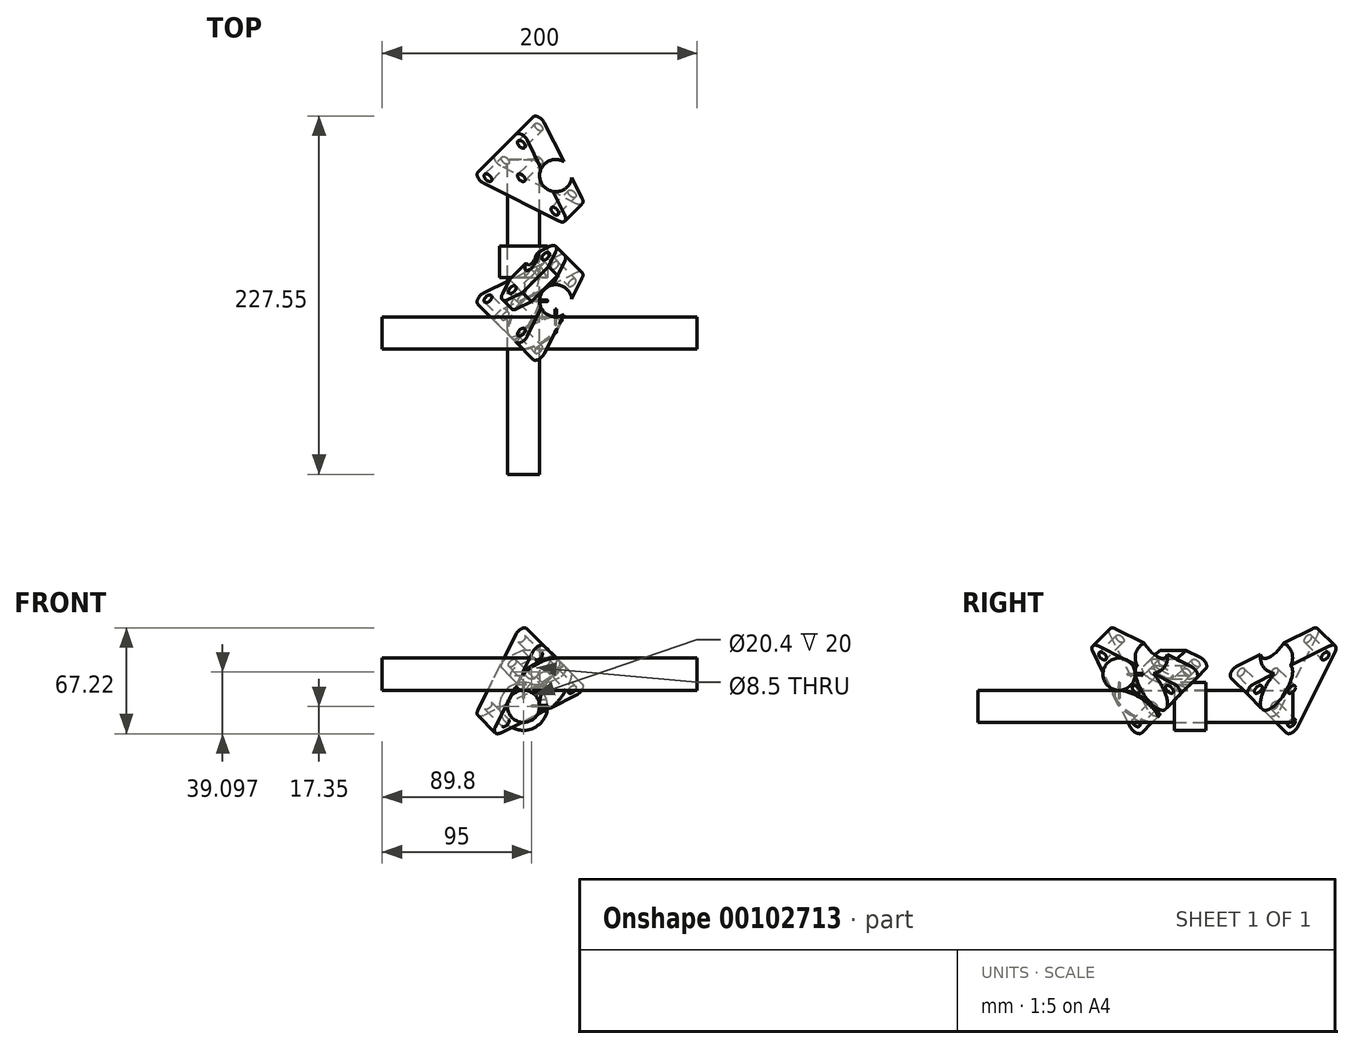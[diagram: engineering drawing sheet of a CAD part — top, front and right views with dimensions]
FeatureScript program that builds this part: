
annotation { "Feature Type Name" : "Feature", "Feature Type Description" : "" }
export const myFeature = defineFeature(function(context is Context, id is Id, definition is map)
    precondition{}
    {
        {
            var Q0;
            Q0=qCreatedBy(makeId("Top.planeOp"),FACE);
            var sketch = newSketch(context, id + "F0", { "sketchPlane" : qUnion([Q0])});
            skCircle(sketch, "E0", {"center": v(10.25, 10.25) * mm, "radius": 10.25 * mm});
            skLineSegment(sketch, "E1", {"start": v(3, 3) * mm, "end": v(14.79, -8.78) * mm, "construction": true});
            skLineSegment(sketch, "E2", {"start": v(30.79, 4.2) * mm, "end": v(17.5, 17.5) * mm, "construction": true});
            skLineSegment(sketch, "E3", {"start": v(0, 0) * mm, "end": v(17.5, 17.5) * mm, "construction": true});
            skLineSegment(sketch, "E4", {"start": v(14.79, -8.78) * mm, "end": v(30.79, 4.2) * mm, "construction": true});
            skSolve(sketch);
        }
        {
            var Q0;
            Q0=qSketchRegion(id+"F0",true);
            extrude(context, id + "F1", {"entities" : qUnion([Q0]), "endBound" : BoundingType.SYMMETRIC, "depth" : 200 * mm});
        }
        {
            var Q0;
            Q0=qCreatedBy(makeId("Right.planeOp"),FACE);
            var sketch = newSketch(context, id + "F2", { "sketchPlane" : qUnion([Q0])});
            skCircle(sketch, "E5", {"center": v(-10.25, 10.25) * mm, "radius": 10.25 * mm});
            skLineSegment(sketch, "E6", {"start": v(0, 0) * mm, "end": v(-17.5, 17.5) * mm, "construction": true});
            skLineSegment(sketch, "E7", {"start": v(-3, 3) * mm, "end": v(-20.36, -14.35) * mm, "construction": true});
            skLineSegment(sketch, "E8", {"start": v(-20.36, -14.35) * mm, "end": v(-34.85, 0.14) * mm, "construction": true});
            skLineSegment(sketch, "E9", {"start": v(-34.85, 0.14) * mm, "end": v(-17.5, 17.5) * mm, "construction": true});
            skSolve(sketch);
        }
        {
            var Q0;
            Q0=qSketchRegion(id+"F2",true);
            extrude(context, id + "F3", {"entities" : qUnion([Q0]), "endBound" : BoundingType.SYMMETRIC, "depth" : 200 * mm});
        }
        {
            var Q0;
            Q0=qCreatedBy(makeId("Front.planeOp"),FACE);
            var sketch = newSketch(context, id + "F4", { "sketchPlane" : qUnion([Q0])});
            skCircle(sketch, "E10", {"center": v(-10.2, -10.2) * mm, "radius": 10.2 * mm});
            skLineSegment(sketch, "E11", {"start": v(0, 0) * mm, "end": v(-17.41, -17.41) * mm, "construction": true});
            skLineSegment(sketch, "E12", {"start": v(-2.99, -2.99) * mm, "end": v(15.73, -21.7) * mm, "construction": true});
            skLineSegment(sketch, "E13", {"start": v(15.73, -21.7) * mm, "end": v(1.3, -36.13) * mm, "construction": true});
            skLineSegment(sketch, "E14", {"start": v(1.3, -36.13) * mm, "end": v(-17.41, -17.41) * mm, "construction": true});
            skSolve(sketch);
        }
        {
            var Q0;
            Q0=qSketchRegion(id+"F4",true);
            extrude(context, id + "F5", {"entities" : qUnion([Q0]), "endBound" : BoundingType.SYMMETRIC, "depth" : 200 * mm});
        }
        {
            var Q0;
            Q0=sQuery(id+"F2.wireOp",VERTEX,"E5.center");
            var Q1;
            Q1=sQuery(id+"F4.wireOp",VERTEX,"E10.center");
            var Q2;
            Q2=sQuery(id+"F0.wireOp",VERTEX,"E0.center");
            cPlane(context, id + "F6", {"entities" : qUnion([Q0, Q1, Q2]), "cplaneType" : CPlaneType.THREE_POINT, "offset" : 150 * mm, "width" : 150 * mm, "height" : 150 * mm});
        }
        {
            var Q0;
            Q0=qCreatedBy(makeId("Top.planeOp"),FACE);
            var sketch = newSketch(context, id + "F7", { "sketchPlane" : qUnion([Q0])});
            skLineSegment(sketch, "E15", {"start": v(-20.4, -100) * mm, "end": v(-20.4, 100) * mm});
            skLineSegment(sketch, "E16", {"start": v(0, 100) * mm, "end": v(0, -100) * mm});
            skLineSegment(sketch, "E17", {"start": v(100, -20.5) * mm, "end": v(-100, -20.5) * mm});
            skLineSegment(sketch, "E18", {"start": v(-100, 0) * mm, "end": v(100, 0) * mm});
            skLineSegment(sketch, "E19", {"start": v(-20.4, -20.5) * mm, "end": v(0, 0) * mm, "construction": true});
            skCircle(sketch, "E20", {"center": v(-10.2, -10.25) * mm, "radius": 0.5 * mm});
            skSolve(sketch);
        }
        {
            var Q0;
            Q0=makeQuery(id+"F7.imprint","IMPRINT",FACE,{"disambiguationData":[TD([[makeQuery(id+"F7.imprint","IMPRINT",EDGE,{"derivedFrom":sQuery(id+"F7.wireOp",EDGE,"E20")}),1.0]])]});
            extrude(context, id + "F8", {"entities" : qUnion([Q0]), "endBound" : BoundingType.SYMMETRIC, "depth" : 10 * mm});
        }
        {
            var Q0;
            Q0=qCreatedBy(makeId("Right.planeOp"),FACE);
            var sketch = newSketch(context, id + "F9", { "sketchPlane" : qUnion([Q0])});
            skLineSegment(sketch, "E21", {"start": v(100, -20.4) * mm, "end": v(-100, -20.4) * mm});
            skLineSegment(sketch, "E22", {"start": v(-100, 0) * mm, "end": v(100, 0) * mm});
            skLineSegment(sketch, "E23", {"start": v(20.5, 100) * mm, "end": v(20.5, -100) * mm});
            skLineSegment(sketch, "E24", {"start": v(0, -100) * mm, "end": v(0, 100) * mm});
            skLineSegment(sketch, "E25", {"start": v(20.5, -20.4) * mm, "end": v(0, 0) * mm, "construction": true});
            skCircle(sketch, "E26", {"center": v(10.25, -10.2) * mm, "radius": 0.5 * mm});
            skSolve(sketch);
        }
        {
            var Q0;
            Q0=makeQuery(id+"F9.imprint","IMPRINT",FACE,{"disambiguationData":[TD([[makeQuery(id+"F9.imprint","IMPRINT",EDGE,{"derivedFrom":sQuery(id+"F9.wireOp",EDGE,"E26")}),1.0]])]});
            extrude(context, id + "F10", {"entities" : qUnion([Q0]), "endBound" : BoundingType.SYMMETRIC, "depth" : 10 * mm});
        }
        {
            var Q0;
            Q0=qCreatedBy(makeId("Front.planeOp"),FACE);
            var sketch = newSketch(context, id + "F11", { "sketchPlane" : qUnion([Q0])});
            skLineSegment(sketch, "E27", {"start": v(0, -100) * mm, "end": v(0, 100) * mm});
            skLineSegment(sketch, "E28", {"start": v(20.5, 100) * mm, "end": v(20.5, -100) * mm});
            skLineSegment(sketch, "E29", {"start": v(-100, 20.5) * mm, "end": v(100, 20.5) * mm});
            skLineSegment(sketch, "E30", {"start": v(100, 0) * mm, "end": v(-100, 0) * mm});
            skLineSegment(sketch, "E31", {"start": v(0, 0) * mm, "end": v(20.5, 20.5) * mm, "construction": true});
            skCircle(sketch, "E32", {"center": v(10.25, 10.25) * mm, "radius": 0.5 * mm});
            skSolve(sketch);
        }
        {
            var Q0;
            Q0=makeQuery(id+"F11.imprint","IMPRINT",FACE,{"disambiguationData":[TD([[makeQuery(id+"F11.imprint","IMPRINT",EDGE,{"derivedFrom":sQuery(id+"F11.wireOp",EDGE,"E32")}),1.0]])]});
            extrude(context, id + "F12", {"entities" : qUnion([Q0]), "endBound" : BoundingType.SYMMETRIC, "depth" : 10 * mm});
        }
        {
            var Q0;
            Q0=qCreatedBy(id+"F6.planeOp",FACE);
            var sketch = newSketch(context, id + "F13", { "sketchPlane" : qUnion([Q0])});
            skLineSegment(sketch, "E33", {"start": v(0, 44) * mm, "end": v(0, -22) * mm, "construction": true});
            skLineSegment(sketch, "E34", {"start": v(0, 44) * mm, "end": v(-38.1, -22) * mm});
            skLineSegment(sketch, "E35", {"start": v(-38.1, -22) * mm, "end": v(38.1, -22) * mm});
            skLineSegment(sketch, "E36", {"start": v(38.1, -22) * mm, "end": v(0, 44) * mm});
            skLineSegment(sketch, "E37", {"start": v(-38.1, -22) * mm, "end": v(19.05, 11) * mm, "construction": true});
            skLineSegment(sketch, "E38", {"start": v(38.1, -22) * mm, "end": v(-19.05, 11) * mm, "construction": true});
            skCircle(sketch, "E39", {"center": v(0, 0) * mm, "radius": 3.05 * mm});
            skCircle(sketch, "E40", {"center": v(0, 30) * mm, "radius": 3.05 * mm});
            skCircle(sketch, "E41", {"center": v(-25.98, -15) * mm, "radius": 3.05 * mm});
            skCircle(sketch, "E42", {"center": v(25.98, -15) * mm, "radius": 3.05 * mm});
            skSolve(sketch);
        }
        {
            var Q0;
            Q0=qSketchRegion(id+"F13",true);
            extrude(context, id + "F14", {"entities" : qUnion([Q0]), "depth" : 20 * mm});
        }
        {
            var Q0;
            Q0=makeQuery(id+"F1.opExtrude","SWEPT_BODY",BODY,{"disambiguationData":[OSD([sQuery(id+"F0.wireOp",EDGE,"E0")])]});
            var Q1;
            Q1=makeQuery(id+"F14.opExtrude","SWEPT_BODY",BODY,{"disambiguationData":[OSD([sQuery(id+"F13.wireOp",EDGE,"E34"),sQuery(id+"F13.wireOp",EDGE,"E35"),sQuery(id+"F13.wireOp",EDGE,"E36"),sQuery(id+"F13.wireOp",EDGE,"E39"),sQuery(id+"F13.wireOp",EDGE,"E40"),sQuery(id+"F13.wireOp",EDGE,"E41"),sQuery(id+"F13.wireOp",EDGE,"E42")])]});
            booleanBodies(context, id + "F15", {"operationType" : BooleanOperationType.SUBTRACTION, "tools" : qUnion([Q0]), "targets" : qUnion([Q1])});
        }
        {
            var Q0;
            Q0=makeQuery(id+"F14.opExtrude","SWEPT_EDGE",EDGE,{"disambiguationData":[OSD([sQuery(id+"F13.wireOp",EDGE,"E34"),sQuery(id+"F13.wireOp",EDGE,"E36")])]});
            var Q1;
            Q1=makeQuery(id+"F14.opExtrude","SWEPT_EDGE",EDGE,{"disambiguationData":[OSD([sQuery(id+"F13.wireOp",EDGE,"E35"),sQuery(id+"F13.wireOp",EDGE,"E36")])]});
            var Q2;
            Q2=makeQuery(id+"F14.opExtrude","SWEPT_EDGE",EDGE,{"disambiguationData":[OSD([sQuery(id+"F13.wireOp",EDGE,"E34"),sQuery(id+"F13.wireOp",EDGE,"E35")])]});
            fillet(context, id + "F16", {"entities" : qUnion([Q0, Q1, Q2]), "radius" : 5 * mm, "tangentPropagation" : true, "allowEdgeOverflow" : false});
        }
        {
            var Q0;
            Q0=makeQuery(id+"F13.imprint","IMPRINT",FACE,{"disambiguationData":[TD([[makeQuery(id+"F13.imprint","IMPRINT",EDGE,{"derivedFrom":sQuery(id+"F13.wireOp",EDGE,"E34")}),1.0]])]});
            extrude(context, id + "F17", {"entities" : qUnion([Q0]), "operationType" : NewBodyOperationType.REMOVE, "depth" : 1 * mm});
        }
        {
            var Q0;
            Q0=makeQuery(id+"F14.opExtrude","SWEPT_BODY",BODY,{"disambiguationData":[OSD([sQuery(id+"F13.wireOp",EDGE,"E34"),sQuery(id+"F13.wireOp",EDGE,"E35"),sQuery(id+"F13.wireOp",EDGE,"E36"),sQuery(id+"F13.wireOp",EDGE,"E39"),sQuery(id+"F13.wireOp",EDGE,"E40"),sQuery(id+"F13.wireOp",EDGE,"E41"),sQuery(id+"F13.wireOp",EDGE,"E42")])]});
            var Q1;
            Q1=qCreatedBy(makeId("Front.planeOp"),FACE);
            mirror(context, id + "F18", {"entities" : qUnion([Q0]), "mirrorPlane" : qUnion([Q1])});
        }
        {
            var Q0;
            Q0=makeQuery(id+"F18.opPattern","COPY",BODY,{"derivedFrom":makeQuery(id+"F14.opExtrude","SWEPT_BODY",BODY,{"disambiguationData":[OSD([sQuery(id+"F13.wireOp",EDGE,"E34"),sQuery(id+"F13.wireOp",EDGE,"E35"),sQuery(id+"F13.wireOp",EDGE,"E36"),sQuery(id+"F13.wireOp",EDGE,"E39"),sQuery(id+"F13.wireOp",EDGE,"E40"),sQuery(id+"F13.wireOp",EDGE,"E41"),sQuery(id+"F13.wireOp",EDGE,"E42")])]}),"instanceName":"1"});
            transform(context, id + "F19", {"entities" : qUnion([Q0]), "transformType" : TransformType.TRANSLATION_3D, "dx" : 0 * mm, "dy" : 100 * mm, "dz" : 0 * mm, "makeCopy" : false});
        }
        {
            var Q0;
            Q0=qCreatedBy(makeId("Front.planeOp"),FACE);
            cPlane(context, id + "F20", {"entities" : qUnion([Q0]), "cplaneType" : CPlaneType.OFFSET, "offset" : 25 * mm, "oppositeDirection" : true, "width" : 150 * mm, "height" : 150 * mm});
        }
        {
            var Q0;
            Q0=qCreatedBy(id+"F20.planeOp",FACE);
            var sketch = newSketch(context, id + "F21", { "sketchPlane" : qUnion([Q0])});
            skArc(sketch, "E43.0", {"start": v(-5.66, -1.07) * mm, "mid": v(-14.76, -1.08) * mm, "end": v(-20.23, -8.35) * mm});
            skArc(sketch, "E44", {"start": v(-20.23, -8.35) * mm, "mid": v(-5.64, -19.32) * mm, "end": v(-5.66, -1.07) * mm});
            skCircle(sketch, "E45", {"center": v(-10.2, -10.2) * mm, "radius": 15.2 * mm});
            skSolve(sketch);
        }
        {
            var Q0;
            Q0=qSketchRegion(id+"F21",true);
            extrude(context, id + "F22", {"entities" : qUnion([Q0]), "oppositeDirection" : true, "depth" : 20 * mm});
        }
        {
            var Q0;
            Q0=makeQuery(id+"F14.opExtrude","SWEPT_BODY",BODY,{"disambiguationData":[OSD([sQuery(id+"F13.wireOp",EDGE,"E34"),sQuery(id+"F13.wireOp",EDGE,"E35"),sQuery(id+"F13.wireOp",EDGE,"E36"),sQuery(id+"F13.wireOp",EDGE,"E39"),sQuery(id+"F13.wireOp",EDGE,"E40"),sQuery(id+"F13.wireOp",EDGE,"E41"),sQuery(id+"F13.wireOp",EDGE,"E42")])]});
            var Q1;
            Q1=makeQuery(id+"F22.opExtrude","SWEPT_BODY",BODY,{"disambiguationData":[OSD([sQuery(id+"F21.wireOp",EDGE,"E43.0"),sQuery(id+"F21.wireOp",EDGE,"E44"),sQuery(id+"F21.wireOp",EDGE,"E45")])]});
            booleanBodies(context, id + "F23", {"operationType" : BooleanOperationType.SUBTRACTION, "tools" : qUnion([Q0]), "targets" : qUnion([Q1]), "keepTools" : true});
        }
        {
            var Q0;
            Q0=makeQuery(id+"F14.opExtrude","CAP_FACE",FACE,{"disambiguationData":[OSD([sQuery(id+"F13.wireOp",EDGE,"E34"),sQuery(id+"F13.wireOp",EDGE,"E35"),sQuery(id+"F13.wireOp",EDGE,"E36"),sQuery(id+"F13.wireOp",EDGE,"E39"),sQuery(id+"F13.wireOp",EDGE,"E40"),sQuery(id+"F13.wireOp",EDGE,"E41"),sQuery(id+"F13.wireOp",EDGE,"E42")])],"isStart":false});
            var sketch = newSketch(context, id + "F24", { "sketchPlane" : qUnion([Q0])});
            skLineSegment(sketch, "E46", {"start": v(-25.98, -15) * mm, "end": v(0, 0) * mm, "construction": true});
            skPoint(sketch, "E47", {"position": v(-13, -7.5) * mm});
            skCircle(sketch, "E48.0", {"center": v(-25.98, -15) * mm, "radius": 3.05 * mm});
            skCircle(sketch, "E49.0", {"center": v(0, 0) * mm, "radius": 3.05 * mm});
            skLineSegment(sketch, "E50", {"start": v(-18.1, -22) * mm, "end": v(2.12, -10.32) * mm});
            skLineSegment(sketch, "E51", {"start": v(-25.98, -15) * mm, "end": v(-31.22, -18.03) * mm, "construction": true});
            skLineSegment(sketch, "E52", {"start": v(0, 0) * mm, "end": v(5.24, 3.03) * mm, "construction": true});
            skLineSegment(sketch, "E53.MirrorCS", {"start": v(-28.1, -4.68) * mm, "end": v(-7.88, 7) * mm});
            skArc(sketch, "E54.0", {"start": v(-33.77, -14.5) * mm, "mid": v(-33.77, -19.5) * mm, "end": v(-29.44, -22) * mm});
            skLineSegment(sketch, "E55", {"start": v(-13, -7.5) * mm, "end": v(-10.48, -11.84) * mm, "construction": true});
            skArc(sketch, "E56.MirrorCS", {"start": v(3.46, 7) * mm, "mid": v(7.8, 4.5) * mm, "end": v(7.8, -0.5) * mm});
            skLineSegment(sketch, "E57.0", {"start": v(-29.44, -22) * mm, "end": v(-18.1, -22) * mm});
            skLineSegment(sketch, "E58.0", {"start": v(-28.1, -4.68) * mm, "end": v(-33.77, -14.5) * mm});
            skPoint(sketch, "E59.orphan", {"position": v(-7.2, -22) * mm});
            skPoint(sketch, "E60.orphan", {"position": v(-24.43, 1.68) * mm});
            skLineSegment(sketch, "E61.MirrorCS", {"start": v(7.8, -0.5) * mm, "end": v(2.12, -10.32) * mm});
            skLineSegment(sketch, "E62.MirrorCS", {"start": v(-7.88, 7) * mm, "end": v(3.46, 7) * mm});
            skSolve(sketch);
        }
        {
            var Q0;
            Q0=qCreatedBy(makeId("Front.planeOp"),FACE);
            var Q1;
            Q1=sQuery(id+"F24.wireOp",VERTEX,"E47");
            cPlane(context, id + "F25", {"entities" : qUnion([Q0, Q1]), "cplaneType" : CPlaneType.PLANE_POINT, "offset" : 150 * mm, "width" : 150 * mm, "height" : 150 * mm});
        }
        {
            var Q0;
            Q0=qCreatedBy(id+"F25.planeOp",FACE);
            var sketch = newSketch(context, id + "F26", { "sketchPlane" : qUnion([Q0])});
            skPoint(sketch, "E63.0", {"position": v(-5, 11.55) * mm});
            skCircle(sketch, "E64", {"center": v(-5, 11.55) * mm, "radius": 4.25 * mm});
            skLineSegment(sketch, "E65.0", {"start": v(9.67, 11.55) * mm, "end": v(-11.55, 11.55) * mm});
            skSolve(sketch);
        }
        {
            var Q0;
            Q0=qSketchRegion(id+"F26",true);
            extrude(context, id + "F27", {"entities" : qUnion([Q0]), "endBound" : BoundingType.SYMMETRIC, "depth" : 100 * mm});
        }
        {
            var Q0;
            Q0=qSketchRegion(id+"F24",true);
            extrude(context, id + "F28", {"entities" : qUnion([Q0]), "depth" : 10 * mm});
        }
        {
            var Q0;
            Q0=makeQuery(id+"F27.opExtrude","SWEPT_BODY",BODY,{"disambiguationData":[OSD([sQuery(id+"F26.wireOp",EDGE,"E64")])]});
            var Q1;
            Q1=makeQuery(id+"F28.opExtrude","SWEPT_BODY",BODY,{"disambiguationData":[OSD([sQuery(id+"F24.wireOp",EDGE,"E48.0"),sQuery(id+"F24.wireOp",EDGE,"E49.0"),sQuery(id+"F24.wireOp",EDGE,"E50"),sQuery(id+"F24.wireOp",EDGE,"ihNIrliq-H3R9-TWVr-Ra94-1WiVHtPCXJTJ"),sQuery(id+"F24.wireOp",EDGE,"GkEZTfjY-Z4Tu-wNJf-vkro-SwpSQShDt9Xh"),sQuery(id+"F24.wireOp",EDGE,"a0bdbbf2-04d8-44a9-b0fc-b3eed8f7528f0.MirrorCS"),sQuery(id+"F24.wireOp",EDGE,"E53.MirrorCS"),sQuery(id+"F24.wireOp",EDGE,"ff99dd6a-50c1-4e35-a48b-94fbbe8486440.MirrorCS")])]});
            booleanBodies(context, id + "F29", {"operationType" : BooleanOperationType.SUBTRACTION, "tools" : qUnion([Q0]), "targets" : qUnion([Q1])});
        }
    });
